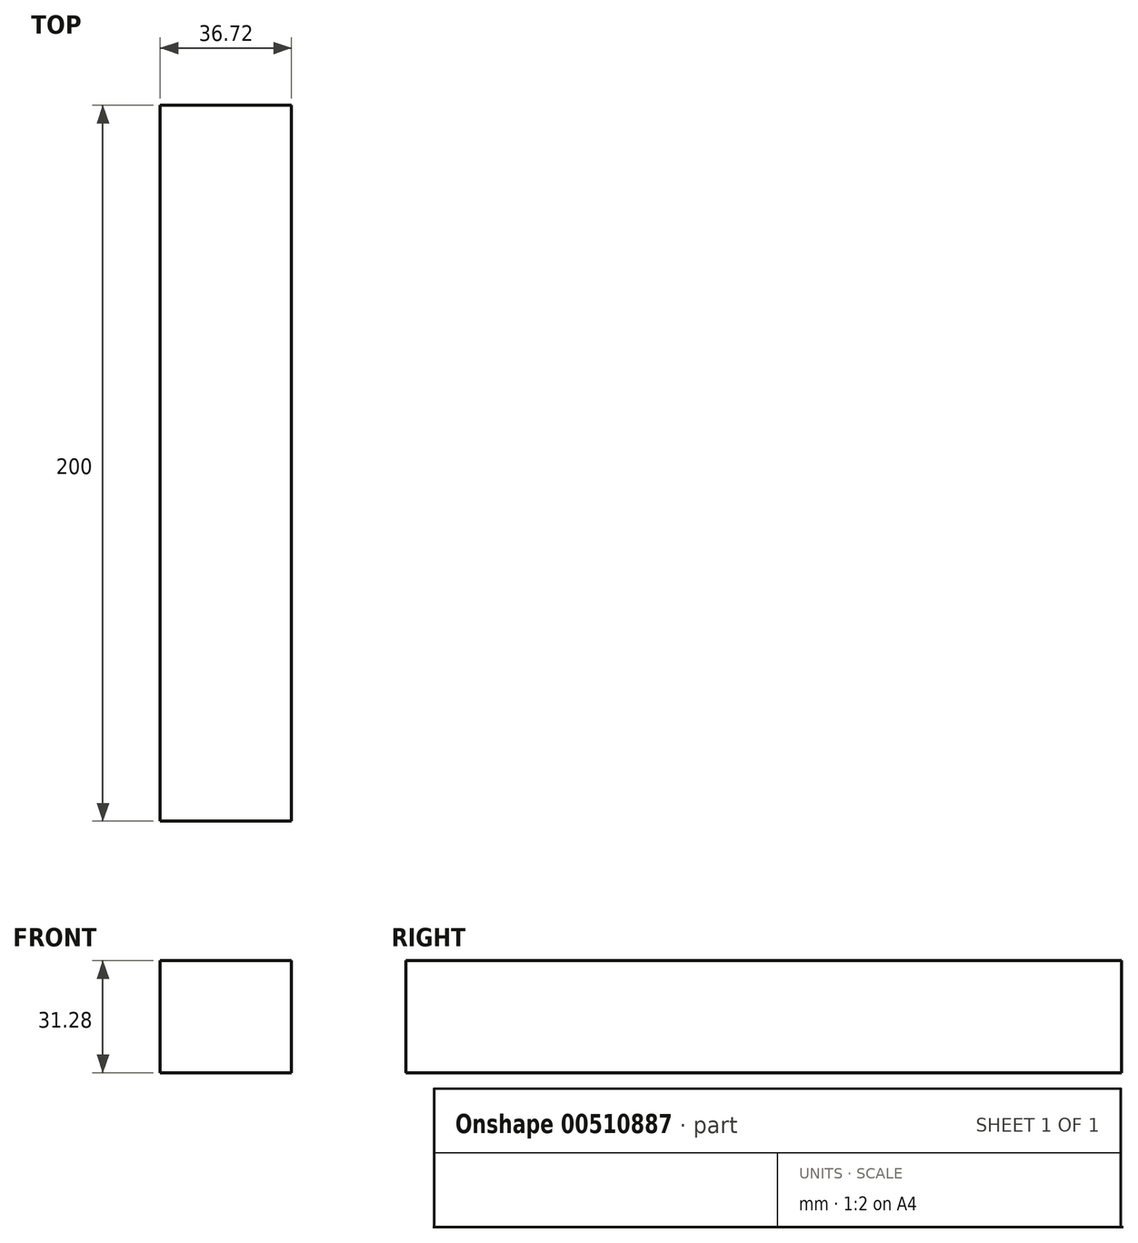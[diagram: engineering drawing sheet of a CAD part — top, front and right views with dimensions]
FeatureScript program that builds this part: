
annotation { "Feature Type Name" : "Feature", "Feature Type Description" : "" }
export const myFeature = defineFeature(function(context is Context, id is Id, definition is map)
    precondition{}
    {
        {
            var Q0;
            Q0=qCreatedBy(makeId("Front.planeOp"),FACE);
            var sketch = newSketch(context, id + "F0", { "sketchPlane" : qUnion([Q0])});
            skLineSegment(sketch, "E0.bottom", {"start": v(-15.5, -15.64) * mm, "end": v(21.23, -15.64) * mm});
            skLineSegment(sketch, "E0.top", {"start": v(-15.5, 15.64) * mm, "end": v(21.23, 15.64) * mm});
            skLineSegment(sketch, "E0.left", {"start": v(-15.5, -15.64) * mm, "end": v(-15.5, 15.64) * mm});
            skLineSegment(sketch, "E0.right", {"start": v(21.23, -15.64) * mm, "end": v(21.23, 15.64) * mm});
            skPoint(sketch, "E0.middle", {"position": v(2.87, 0) * mm});
            skSolve(sketch);
        }
        {
            var Q0;
            Q0=qSketchRegion(id+"F0",true);
            extrude(context, id + "F1", {"entities" : qUnion([Q0]), "depth" : 200 * mm});
        }
    });
